# Revit family: Plania Benches
name_source: partatom
category: Furniture
units: mm (PartAtom-declared; Revit-internal decimal feet)

## family parameters
Always vertical = Yes
Cut with Voids When Loaded = No
OmniClass Number = 23.40.20.00
OmniClass Title = General Furniture and Specialties
Room Calculation Point = No
Shared = No
Work Plane-Based = No

## types (12) — shared parameters
Depth = 480 mm  [stored 1.5748 ft]
Frame = Epoxy - M1_B00 - Black
Manufacturer = Sandler
Seat = Fabric - Mainline Flax - Waterloo MLF21
URL = https://www.sandlerseating.com
zero-valued in all types: Default Elevation

## per-type parameters (varying)
| type | BackSupportNum | Description | Height | IsVisible | Width |
| PL70012 | 2 | Upholstered 48″ bench seat inclusive of Plania frame. This seat needs 2 trestle legs to be ordered separately, assembly required. | 450 mm  [stored 1.47638 ft] | No | 1200 mm  [stored 3.93701 ft] |
| PL70016 | 2 | Upholstered 63″ bench seat inclusive of Plania frame. This seat needs 2 trestle legs to be ordered separately, assembly required. | 450 mm  [stored 1.47638 ft] | No | 1600 mm  [stored 5.24934 ft] |
| PL70018 | 2 | Upholstered 70″ bench seat inclusive of Plania frame. This seat needs 2 trestle legs to be ordered separately, assembly required. | 450 mm  [stored 1.47638 ft] | No | 1800 mm  [stored 5.90551 ft] |
| PL70020 | 2 | Upholstered 80″ bench seat inclusive of Plania frame. This seat needs 2 trestle legs to be ordered separately, assembly required. | 450 mm  [stored 1.47638 ft] | No | 2000 mm  [stored 6.56168 ft] |
| PL70024 | 2 | Upholstered 95″ bench seat inclusive of Plania frame. This seat needs 2 trestle legs to be ordered separately, assembly required. | 450 mm  [stored 1.47638 ft] | No | 2400 mm |
| PL70028 | 2 | Upholstered 110″ bench seat inclusive of Plania frame. This seat needs 2 trestle legs to be ordered separately, assembly required. | 450 mm  [stored 1.47638 ft] | No | 2800 mm  [stored 9.18635 ft] |
| PL70212 | 2 | Upholstered 48″ bench seat & back inclusive of Plania frame. This seat needs 2 trestle legs to be ordered separately, assembly required. | 825 mm  [stored 2.70669 ft] | Yes | 1200 mm  [stored 3.93701 ft] |
| PL70216 | 2 | Upholstered 63″ bench seat & back inclusive of Plania frame. This seat needs 2 trestle legs to be ordered separately, assembly required. | 825 mm  [stored 2.70669 ft] | Yes | 1600 mm  [stored 5.24934 ft] |
| PL70218 | 3 | Upholstered 70″ bench seat & back inclusive of Plania frame. This seat needs 2 trestle legs to be ordered separately, assembly required. | 825 mm  [stored 2.70669 ft] | Yes | 1800 mm  [stored 5.90551 ft] |
| PL70220 | 3 | Upholstered 80″ bench seat & back inclusive of Plania frame. This seat needs 2 trestle legs to be ordered separately, assembly required. | 825 mm  [stored 2.70669 ft] | Yes | 2000 mm  [stored 6.56168 ft] |
| PL70224 | 3 | Upholstered 95″ bench seat & back inclusive of Plania frame. This seat needs 2 trestle legs to be ordered separately, assembly required. | 825 mm  [stored 2.70669 ft] | Yes | 2400 mm |
| PL70228 | 3 | Upholstered 110″ bench seat & back inclusive of Plania frame. This seat needs 3 trestle legs to be ordered separately, assembly required. | 825 mm  [stored 2.70669 ft] | Yes | 2800 mm  [stored 9.18635 ft] |

note: column(s) folded — value = type name in every type: Model

note: [stored X ft] marks values corroborated as IEEE doubles in the binary element streams (Revit-internal decimal feet)

## geometry (parser evidence)
native form markers: Sweep x4
no freeform markers — native parametric forms only
